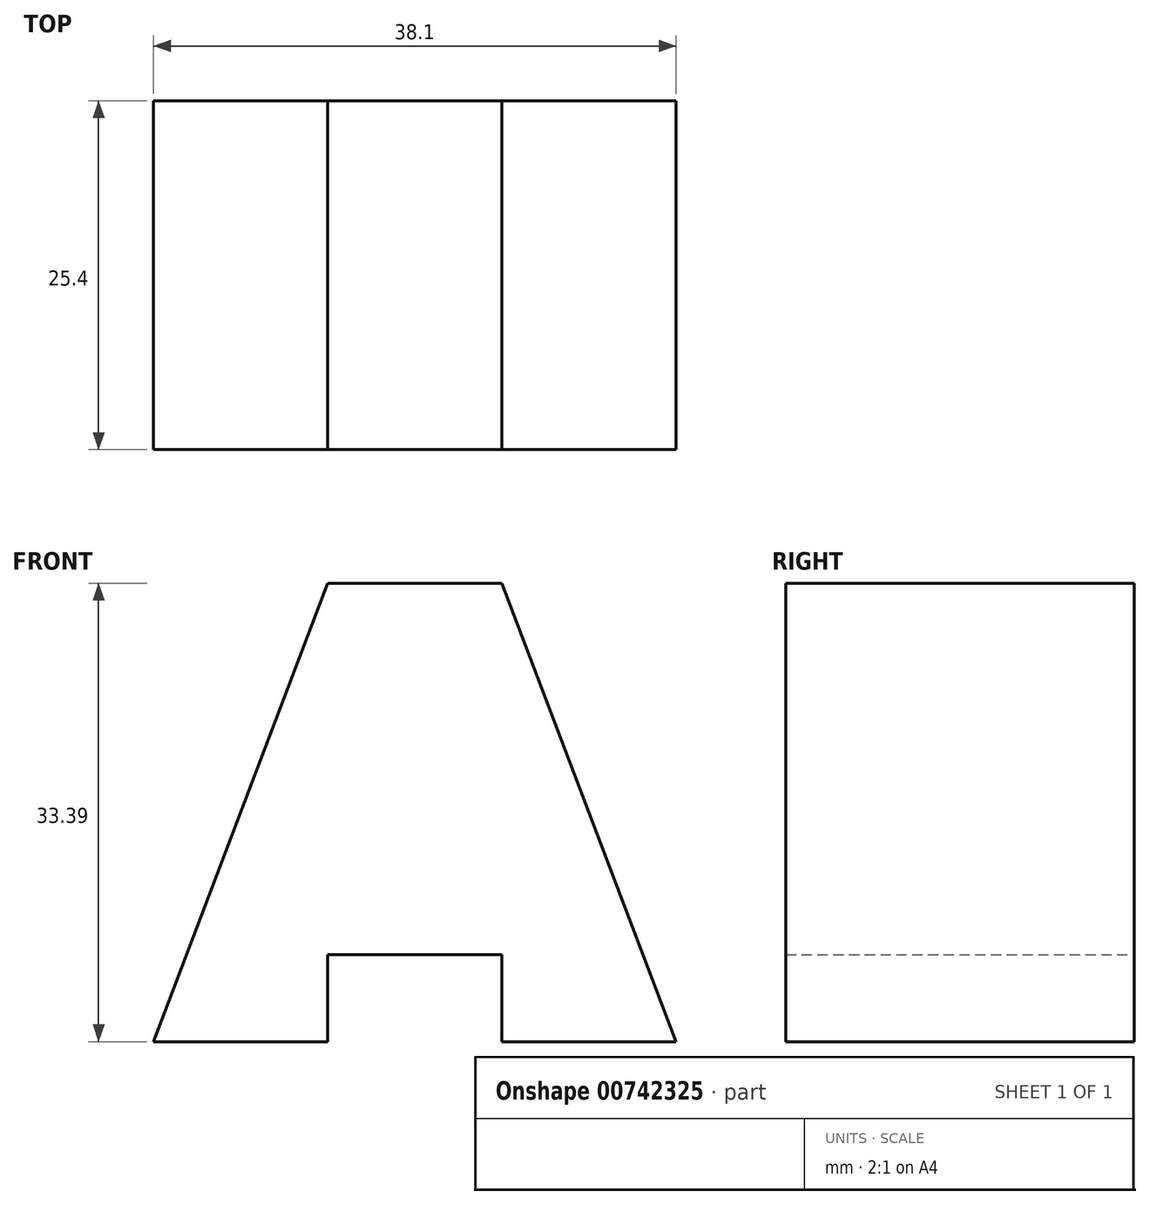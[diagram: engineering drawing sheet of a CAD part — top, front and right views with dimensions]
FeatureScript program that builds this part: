
annotation { "Feature Type Name" : "Feature", "Feature Type Description" : "" }
export const myFeature = defineFeature(function(context is Context, id is Id, definition is map)
    precondition{}
    {
        {
            var Q0;
            Q0=qCreatedBy(makeId("Front.planeOp"),FACE);
            var sketch = newSketch(context, id + "F0", { "sketchPlane" : qUnion([Q0])});
            skLineSegment(sketch, "E0", {"start": v(0, 0) * mm, "end": v(-12.7, 0) * mm});
            skLineSegment(sketch, "E1", {"start": v(-12.7, 0) * mm, "end": v(-12.7, 6.35) * mm});
            skLineSegment(sketch, "E2", {"start": v(-12.7, 6.35) * mm, "end": v(-25.4, 6.35) * mm});
            skLineSegment(sketch, "E3", {"start": v(-25.4, 6.35) * mm, "end": v(-25.4, 0) * mm});
            skLineSegment(sketch, "E4", {"start": v(-25.4, 0) * mm, "end": v(-38.1, 0) * mm});
            skLineSegment(sketch, "E5", {"start": v(-38.1, 0) * mm, "end": v(-25.4, 33.39) * mm});
            skLineSegment(sketch, "E6", {"start": v(-25.4, 33.39) * mm, "end": v(-12.7, 33.39) * mm});
            skLineSegment(sketch, "E7", {"start": v(-12.7, 33.39) * mm, "end": v(0, 0) * mm});
            skSolve(sketch);
        }
        {
            var Q0;
            Q0 = qSketchRegion(id + "F0", true);
            extrude(context, id + "F1", {"entities" : qUnion([Q0]), "depth" : 25.4 * mm, "offsetDistance" : 25.4 * mm});
        }
    });
